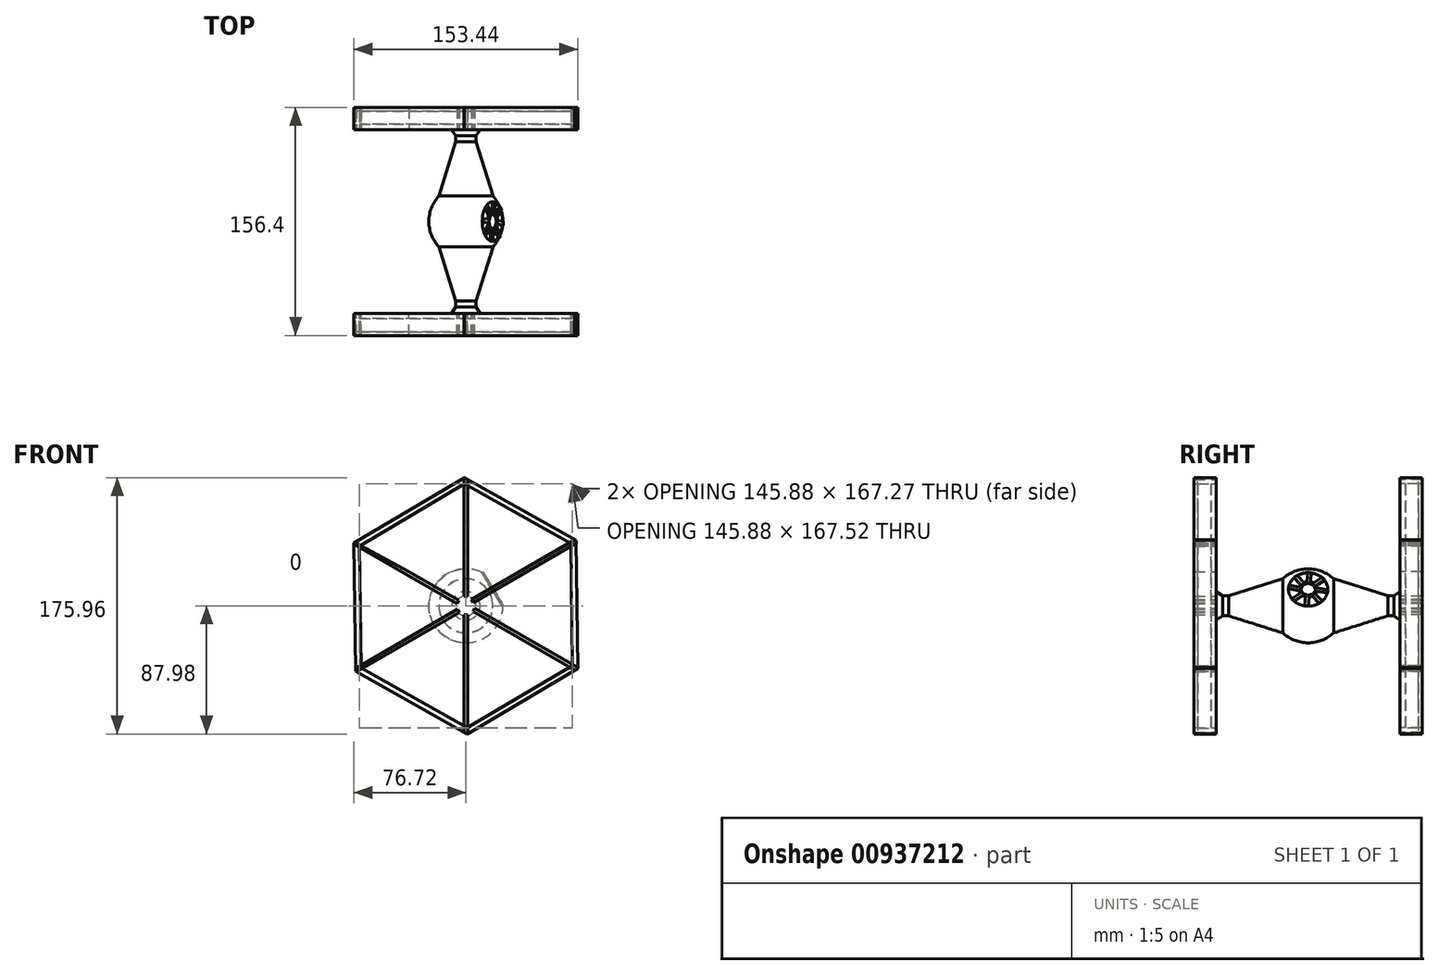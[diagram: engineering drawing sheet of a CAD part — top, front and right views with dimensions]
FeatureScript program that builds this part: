
annotation { "Feature Type Name" : "Feature", "Feature Type Description" : "" }
export const myFeature = defineFeature(function(context is Context, id is Id, definition is map)
    precondition{}
    {
        {
            var Q0;
            Q0=qCreatedBy(makeId("Front.planeOp"),FACE);
            var sketch = newSketch(context, id + "F0", { "sketchPlane" : qUnion([Q0])});
            skArc(sketch, "E0", {"start": v(0, 25.4) * mm, "mid": v(25.4, 0) * mm, "end": v(0, -25.4) * mm});
            skLineSegment(sketch, "E1", {"start": v(0, 25.4) * mm, "end": v(0, -25.4) * mm});
            skSolve(sketch);
        }
        {
            var Q0;
            Q0=qSketchRegion(id+"F0",true);
            var Q1;
            Q1=sQuery(id+"F0.wireOp",EDGE,"E1");
            revolve(context, id + "F1", {"surfaceOperationType" : NewSurfaceOperationType.NEW, "entities" : qUnion([Q0]), "axis" : qUnion([Q1]), "revolveType" : RevolveType.ONE_DIRECTION, "angle" : 180 * degree});
        }
        {
            var Q0;
            Q0=qCreatedBy(makeId("Right.planeOp"),FACE);
            var sketch = newSketch(context, id + "F2", { "sketchPlane" : qUnion([Q0])});
            skLineSegment(sketch, "E2", {"start": v(-62.96, 0) * mm, "end": v(0, 0) * mm});
            skLineSegment(sketch, "E3", {"start": v(-62.96, 0) * mm, "end": v(-62.96, 6.88) * mm});
            skFitSpline(sketch, "E4", {"points": [v(-62.96, 6.88) * mm, v(-54.61, 6.88) * mm, v(-33.5, 12.3) * mm, v(-17.49, 18.56) * mm], "startDerivative": vector(29.42, -2.61) * mm, "endDerivative": vector(41.74, 17.6) * mm});
            skLineSegment(sketch, "E5", {"start": v(-17.49, 18.56) * mm, "end": v(-17.49, 0) * mm});
            skLineSegment(sketch, "E6", {"start": v(-54.61, 6.88) * mm, "end": v(-17.49, 18.56) * mm});
            skLineSegment(sketch, "E7", {"start": v(-54.61, 6.88) * mm, "end": v(-62.96, 6.88) * mm});
            skLineSegment(sketch, "E8", {"start": v(-58.78, 6.88) * mm, "end": v(-62.96, 9.72) * mm});
            skLineSegment(sketch, "E9", {"start": v(-62.96, 6.88) * mm, "end": v(-62.96, 9.72) * mm});
            skSolve(sketch);
        }
        {
            var Q0;
            Q0=qSketchRegion(id+"F2",true);
            var Q1;
            Q1=sQuery(id+"F2.wireOp",EDGE,"E2");
            revolve(context, id + "F3", {"operationType" : NewBodyOperationType.ADD, "surfaceOperationType" : NewSurfaceOperationType.NEW, "entities" : qUnion([Q0]), "axis" : qUnion([Q1]), "revolveType" : RevolveType.FULL});
        }
        {
            var Q0;
            Q0=qCreatedBy(makeId("Front.planeOp"),FACE);
            var sketch = newSketch(context, id + "F4", { "sketchPlane" : qUnion([Q0])});
            skLineSegment(sketch, "E10", {"start": v(18.07, 11.14) * mm, "end": v(0, 0) * mm});
            skSolve(sketch);
        }
        {
            var Q0;
            Q0=makeQuery(id+"F3.opRevolve","SWEPT_FACE",FACE,{"disambiguationData":[OSD([sQuery(id+"F2.wireOp",EDGE,"E3")])]});
            cPlane(context, id + "F5", {"entities" : qUnion([Q0]), "cplaneType" : CPlaneType.OFFSET, "offset" : 0 * mm, "width" : 152.4 * mm, "height" : 152.4 * mm});
        }
        {
            var Q0;
            Q0=qCreatedBy(id+"F5.planeOp",FACE);
            var sketch = newSketch(context, id + "F6", { "sketchPlane" : qUnion([Q0])});
            skCircle(sketch, "E11.cCircle", {"center": v(0, 0) * mm, "radius": 76.2 * mm, "construction": true});
            skLineSegment(sketch, "E11.0", {"start": v(76.62, -43.26) * mm, "end": v(0.84, -87.98) * mm});
            skLineSegment(sketch, "E11.1", {"start": v(0.84, -87.98) * mm, "end": v(-75.78, -44.72) * mm});
            skLineSegment(sketch, "E11.2", {"start": v(-75.78, -44.72) * mm, "end": v(-76.62, 43.26) * mm});
            skLineSegment(sketch, "E11.3", {"start": v(-76.62, 43.26) * mm, "end": v(-0.84, 87.98) * mm});
            skLineSegment(sketch, "E11.4", {"start": v(-0.84, 87.98) * mm, "end": v(75.78, 44.72) * mm});
            skLineSegment(sketch, "E11.5", {"start": v(75.78, 44.72) * mm, "end": v(76.62, -43.26) * mm});
            skPoint(sketch, "E11.0.midPoint", {"position": v(38.73, -65.62) * mm});
            skSolve(sketch);
        }
        {
            var Q0;
            Q0=qSketchRegion(id+"F6",true);
            extrude(context, id + "F7", {"entities" : qUnion([Q0]), "depth" : 12.7 * mm, "offsetDistance" : 25.4 * mm});
        }
        {
            var Q0;
            Q0=makeQuery(id+"F7.opExtrude","CAP_FACE",FACE,{"disambiguationData":[OSD([sQuery(id+"F6.wireOp",EDGE,"E11.0"),sQuery(id+"F6.wireOp",EDGE,"E11.1"),sQuery(id+"F6.wireOp",EDGE,"E11.2"),sQuery(id+"F6.wireOp",EDGE,"E11.3"),sQuery(id+"F6.wireOp",EDGE,"E11.4"),sQuery(id+"F6.wireOp",EDGE,"E11.5")])],"isStart":false});
            shell(context, id + "F8", {"entities" : qUnion([Q0]), "thickness" : 3.66 * mm});
        }
        {
            var Q0;
            Q0=qCreatedBy(id+"F5.planeOp",FACE);
            var sketch = newSketch(context, id + "F9", { "sketchPlane" : qUnion([Q0])});
            skLineSegment(sketch, "E12", {"start": v(0, 92.99) * mm, "end": v(0, 6.47) * mm, "construction": true});
            skLineSegment(sketch, "E13", {"start": v(-80.5, 45.9) * mm, "end": v(-5.53, 2.72) * mm, "construction": true});
            skLineSegment(sketch, "E14", {"start": v(5.53, -2.69) * mm, "end": v(80.5, -45.88) * mm, "construction": true});
            skLineSegment(sketch, "E15", {"start": v(0, -6.03) * mm, "end": v(0, -92.55) * mm});
            skLineSegment(sketch, "E16", {"start": v(-80, -46.75) * mm, "end": v(-5.12, -3.4) * mm, "construction": true});
            skLineSegment(sketch, "E17", {"start": v(4.34, 3.22) * mm, "end": v(79.21, 46.57) * mm, "construction": true});
            skLineSegment(sketch, "E18", {"start": v(-1.27, -6.03) * mm, "end": v(1.27, -6.03) * mm});
            skLineSegment(sketch, "E19", {"start": v(4.9, -3.79) * mm, "end": v(6.17, -1.59) * mm});
            skLineSegment(sketch, "E20", {"start": v(3.7, 4.32) * mm, "end": v(4.97, 2.12) * mm});
            skLineSegment(sketch, "E21", {"start": v(3.7, 4.32) * mm, "end": v(78.58, 47.67) * mm});
            skLineSegment(sketch, "E22", {"start": v(4.97, 2.12) * mm, "end": v(79.85, 45.47) * mm});
            skLineSegment(sketch, "E23", {"start": v(-1.27, 6.47) * mm, "end": v(1.27, 6.47) * mm});
            skLineSegment(sketch, "E24", {"start": v(-6.17, 1.62) * mm, "end": v(-4.9, 3.82) * mm});
            skLineSegment(sketch, "E25", {"start": v(-4.4, -4.44) * mm, "end": v(-5.84, -2.36) * mm});
            skLineSegment(sketch, "E26", {"start": v(-4.9, 3.82) * mm, "end": v(-38.95, 23.43) * mm});
            skLineSegment(sketch, "E27", {"start": v(-6.17, 1.62) * mm, "end": v(-81.14, 44.8) * mm});
            skLineSegment(sketch, "E28", {"start": v(-4.4, -4.44) * mm, "end": v(-79.27, -47.8) * mm});
            skLineSegment(sketch, "E29", {"start": v(-5.84, -2.36) * mm, "end": v(-80, -45.29) * mm});
            skLineSegment(sketch, "E30", {"start": v(4.9, -3.79) * mm, "end": v(79.87, -46.98) * mm});
            skLineSegment(sketch, "E31", {"start": v(6.17, -1.59) * mm, "end": v(81.14, -44.78) * mm});
            skLineSegment(sketch, "E32", {"start": v(-1.27, 6.47) * mm, "end": v(-1.27, 92.99) * mm});
            skLineSegment(sketch, "E33", {"start": v(1.27, 6.47) * mm, "end": v(1.27, 92.99) * mm});
            skLineSegment(sketch, "E34", {"start": v(1.27, -6.03) * mm, "end": v(1.27, -92.55) * mm});
            skLineSegment(sketch, "E35", {"start": v(-1.27, -6.03) * mm, "end": v(-1.27, -92.55) * mm});
            skLineSegment(sketch, "E36", {"start": v(1.27, -92.55) * mm, "end": v(0, -92.55) * mm});
            skLineSegment(sketch, "E37", {"start": v(0, -92.55) * mm, "end": v(-1.27, -92.55) * mm});
            skLineSegment(sketch, "E38", {"start": v(81.14, -44.78) * mm, "end": v(80.5, -45.88) * mm});
            skLineSegment(sketch, "E39", {"start": v(79.87, -46.98) * mm, "end": v(80.5, -45.88) * mm});
            skLineSegment(sketch, "E40", {"start": v(79.21, 46.57) * mm, "end": v(79.85, 45.47) * mm});
            skLineSegment(sketch, "E41", {"start": v(79.21, 46.57) * mm, "end": v(78.58, 47.67) * mm});
            skLineSegment(sketch, "E42", {"start": v(1.27, 92.99) * mm, "end": v(0, 92.99) * mm});
            skLineSegment(sketch, "E43", {"start": v(-1.27, 92.99) * mm, "end": v(0, 92.99) * mm});
            skLineSegment(sketch, "E44", {"start": v(0, 92.99) * mm, "end": v(-1.27, 92.99) * mm});
            skLineSegment(sketch, "E45", {"start": v(-81.14, 44.8) * mm, "end": v(-80.5, 45.9) * mm});
            skLineSegment(sketch, "E46", {"start": v(-38.95, 23.43) * mm, "end": v(-80.5, 45.9) * mm});
            skLineSegment(sketch, "E47", {"start": v(-80, -45.29) * mm, "end": v(-80, -46.75) * mm});
            skLineSegment(sketch, "E48", {"start": v(-79.27, -47.8) * mm, "end": v(-80, -46.75) * mm});
            skSolve(sketch);
        }
        {
            var Q0;
            Q0=qSketchRegion(id+"F9",true);
            extrude(context, id + "F10", {"entities" : qUnion([Q0]), "depth" : 15.24 * mm, "offsetDistance" : 25.4 * mm});
        }
        {
            var Q0;
            Q0=qCreatedBy(id+"F5.planeOp",FACE);
            var sketch = newSketch(context, id + "F11", { "sketchPlane" : qUnion([Q0])});
            skCircle(sketch, "E49.cCircle", {"center": v(0, 0) * mm, "radius": 76.2 * mm, "construction": true});
            skLineSegment(sketch, "E49.0", {"start": v(1.03, -87.98) * mm, "end": v(-75.68, -44.89) * mm});
            skLineSegment(sketch, "E49.1", {"start": v(-75.68, -44.89) * mm, "end": v(-76.71, 43.1) * mm});
            skLineSegment(sketch, "E49.2", {"start": v(-76.71, 43.1) * mm, "end": v(-1.03, 87.98) * mm});
            skLineSegment(sketch, "E49.3", {"start": v(-1.03, 87.98) * mm, "end": v(75.68, 44.89) * mm});
            skLineSegment(sketch, "E49.4", {"start": v(75.68, 44.89) * mm, "end": v(76.71, -43.1) * mm});
            skLineSegment(sketch, "E49.5", {"start": v(76.71, -43.1) * mm, "end": v(1.03, -87.98) * mm});
            skPoint(sketch, "E49.0.midPoint", {"position": v(-37.32, -66.43) * mm});
            skCircle(sketch, "E50.cCircle", {"center": v(0, 0) * mm, "radius": 72.43 * mm, "construction": true});
            skLineSegment(sketch, "E50.0", {"start": v(72.94, -40.93) * mm, "end": v(1.03, -83.63) * mm});
            skLineSegment(sketch, "E50.1", {"start": v(1.03, -83.63) * mm, "end": v(-71.92, -42.7) * mm});
            skLineSegment(sketch, "E50.2", {"start": v(-71.92, -42.7) * mm, "end": v(-72.94, 40.93) * mm});
            skLineSegment(sketch, "E50.3", {"start": v(-72.94, 40.93) * mm, "end": v(-1.03, 83.63) * mm});
            skLineSegment(sketch, "E50.4", {"start": v(-1.03, 83.63) * mm, "end": v(71.92, 42.7) * mm});
            skLineSegment(sketch, "E50.5", {"start": v(71.92, 42.7) * mm, "end": v(72.94, -40.93) * mm});
            skPoint(sketch, "E50.0.midPoint", {"position": v(36.98, -62.28) * mm});
            skLineSegment(sketch, "E51", {"start": v(0, 0) * mm, "end": v(-1.03, 83.63) * mm, "construction": true});
            skSolve(sketch);
        }
        {
            var Q0;
            Q0=qSketchRegion(id+"F11",true);
            extrude(context, id + "F12", {"entities" : qUnion([Q0]), "depth" : 15.24 * mm, "offsetDistance" : 25.4 * mm});
        }
        {
            var Q0;
            Q0=qCreatedBy(id+"F5.planeOp",FACE);
            var sketch = newSketch(context, id + "F13", { "sketchPlane" : qUnion([Q0])});
            skCircle(sketch, "E52.cCircle", {"center": v(0, 0) * mm, "radius": 76.2 * mm, "construction": true});
            skLineSegment(sketch, "E52.0", {"start": v(1.05, -87.98) * mm, "end": v(-75.67, -44.9) * mm});
            skLineSegment(sketch, "E52.1", {"start": v(-75.67, -44.9) * mm, "end": v(-76.72, 43.08) * mm});
            skLineSegment(sketch, "E52.2", {"start": v(-76.72, 43.08) * mm, "end": v(-1.05, 87.98) * mm});
            skLineSegment(sketch, "E52.3", {"start": v(-1.05, 87.98) * mm, "end": v(75.67, 44.9) * mm});
            skLineSegment(sketch, "E52.4", {"start": v(75.67, 44.9) * mm, "end": v(76.72, -43.08) * mm});
            skLineSegment(sketch, "E52.5", {"start": v(76.72, -43.08) * mm, "end": v(1.05, -87.98) * mm});
            skPoint(sketch, "E52.0.midPoint", {"position": v(-37.31, -66.44) * mm});
            skCircle(sketch, "E53.cCircle", {"center": v(0, 0) * mm, "radius": 151.68 * mm, "construction": true});
            skLineSegment(sketch, "E53.0", {"start": v(-149.87, -90.64) * mm, "end": v(-153.43, 84.47) * mm});
            skLineSegment(sketch, "E53.1", {"start": v(-153.43, 84.47) * mm, "end": v(-3.56, 175.11) * mm});
            skLineSegment(sketch, "E53.2", {"start": v(-3.56, 175.11) * mm, "end": v(149.87, 90.64) * mm});
            skLineSegment(sketch, "E53.3", {"start": v(149.87, 90.64) * mm, "end": v(153.43, -84.47) * mm});
            skLineSegment(sketch, "E53.4", {"start": v(153.43, -84.47) * mm, "end": v(3.56, -175.11) * mm});
            skLineSegment(sketch, "E53.5", {"start": v(3.56, -175.11) * mm, "end": v(-149.87, -90.64) * mm});
            skPoint(sketch, "E53.0.midPoint", {"position": v(-151.65, -3.09) * mm});
            skSolve(sketch);
        }
        {
            var Q0;
            Q0=qSketchRegion(id+"F13",true);
            extrude(context, id + "F14", {"entities" : qUnion([Q0]), "operationType" : NewBodyOperationType.REMOVE, "depth" : 101.6 * mm, "offsetDistance" : 25.4 * mm});
        }
        {
            var Q0;
            Q0=makeQuery(id+"F1.opRevolve","SWEPT_BODY",BODY,{"disambiguationData":[OSD([sQuery(id+"F0.wireOp",EDGE,"E0"),sQuery(id+"F0.wireOp",EDGE,"E1")])]});
            var Q1;
            Q1=makeQuery(id+"F12.opExtrude","SWEPT_BODY",BODY,{"disambiguationData":[OSD([sQuery(id+"F11.wireOp",EDGE,"E49.0"),sQuery(id+"F11.wireOp",EDGE,"E49.1"),sQuery(id+"F11.wireOp",EDGE,"E49.2"),sQuery(id+"F11.wireOp",EDGE,"E49.3"),sQuery(id+"F11.wireOp",EDGE,"E49.4"),sQuery(id+"F11.wireOp",EDGE,"E49.5"),sQuery(id+"F11.wireOp",EDGE,"E50.0"),sQuery(id+"F11.wireOp",EDGE,"E50.1"),sQuery(id+"F11.wireOp",EDGE,"E50.2"),sQuery(id+"F11.wireOp",EDGE,"E50.3"),sQuery(id+"F11.wireOp",EDGE,"E50.4"),sQuery(id+"F11.wireOp",EDGE,"E50.5")])]});
            var Q2;
            Q2=makeQuery(id+"F10.opExtrude","SWEPT_BODY",BODY,{"disambiguationData":[OSD([sQuery(id+"F9.wireOp",EDGE,"E20"),sQuery(id+"F9.wireOp",EDGE,"E21"),sQuery(id+"F9.wireOp",EDGE,"E22"),sQuery(id+"F9.wireOp",EDGE,"E40"),sQuery(id+"F9.wireOp",EDGE,"E41")])]});
            var Q3;
            Q3=makeQuery(id+"F7.opExtrude","SWEPT_BODY",BODY,{"disambiguationData":[OSD([sQuery(id+"F6.wireOp",EDGE,"E11.0"),sQuery(id+"F6.wireOp",EDGE,"E11.1"),sQuery(id+"F6.wireOp",EDGE,"E11.2"),sQuery(id+"F6.wireOp",EDGE,"E11.3"),sQuery(id+"F6.wireOp",EDGE,"E11.4"),sQuery(id+"F6.wireOp",EDGE,"E11.5")])]});
            var Q4;
            Q4=makeQuery(id+"F10.opExtrude","SWEPT_BODY",BODY,{"disambiguationData":[OSD([sQuery(id+"F9.wireOp",EDGE,"E19"),sQuery(id+"F9.wireOp",EDGE,"E30"),sQuery(id+"F9.wireOp",EDGE,"E31"),sQuery(id+"F9.wireOp",EDGE,"E38"),sQuery(id+"F9.wireOp",EDGE,"E39")])]});
            var Q5;
            Q5=makeQuery(id+"F10.opExtrude","SWEPT_BODY",BODY,{"disambiguationData":[OSD([sQuery(id+"F9.wireOp",EDGE,"E18"),sQuery(id+"F9.wireOp",EDGE,"E34"),sQuery(id+"F9.wireOp",EDGE,"E35"),sQuery(id+"F9.wireOp",EDGE,"E36"),sQuery(id+"F9.wireOp",EDGE,"E37")])]});
            var Q6;
            Q6=makeQuery(id+"F10.opExtrude","SWEPT_BODY",BODY,{"disambiguationData":[OSD([sQuery(id+"F9.wireOp",EDGE,"E24"),sQuery(id+"F9.wireOp",EDGE,"E26"),sQuery(id+"F9.wireOp",EDGE,"E27"),sQuery(id+"F9.wireOp",EDGE,"E45"),sQuery(id+"F9.wireOp",EDGE,"E46")])]});
            var Q7;
            Q7=makeQuery(id+"F10.opExtrude","SWEPT_BODY",BODY,{"disambiguationData":[OSD([sQuery(id+"F9.wireOp",EDGE,"E23"),sQuery(id+"F9.wireOp",EDGE,"E32"),sQuery(id+"F9.wireOp",EDGE,"E33"),sQuery(id+"F9.wireOp",EDGE,"E42"),sQuery(id+"F9.wireOp",EDGE,"E44")])]});
            var Q8;
            Q8=makeQuery(id+"F10.opExtrude","SWEPT_BODY",BODY,{"disambiguationData":[OSD([sQuery(id+"F9.wireOp",EDGE,"E25"),sQuery(id+"F9.wireOp",EDGE,"E28"),sQuery(id+"F9.wireOp",EDGE,"E29"),sQuery(id+"F9.wireOp",EDGE,"E47"),sQuery(id+"F9.wireOp",EDGE,"E48")])]});
            var Q9;
            Q9=qCreatedBy(makeId("Front.planeOp"),FACE);
            mirror(context, id + "F15", {"entities" : qUnion([Q0, Q1, Q2, Q3, Q4, Q5, Q6, Q7, Q8]), "mirrorPlane" : qUnion([Q9])});
        }
        {
            var Q0;
            Q0=sQuery(id+"F4.wireOp",VERTEX,"E10.start");
            var Q1;
            Q1=sQuery(id+"F4.wireOp",EDGE,"E10");
            cPlane(context, id + "F16", {"entities" : qUnion([Q0, Q1]), "cplaneType" : CPlaneType.CURVE_POINT, "offset" : 25.4 * mm, "width" : 152.4 * mm, "height" : 152.4 * mm});
        }
        {
            var Q0;
            Q0=qCreatedBy(id+"F16.planeOp",FACE);
            var sketch = newSketch(context, id + "F17", { "sketchPlane" : qUnion([Q0])});
            skCircle(sketch, "E54", {"center": v(0, 0) * mm, "radius": 13.5 * mm});
            skSolve(sketch);
        }
        {
            var Q0;
            Q0=qSketchRegion(id+"F17",true);
            extrude(context, id + "F18", {"entities" : qUnion([Q0]), "operationType" : NewBodyOperationType.REMOVE, "oppositeDirection" : true, "depth" : 25.4 * mm, "offsetDistance" : 25.4 * mm});
        }
        {
            var Q0;
            Q0=qCreatedBy(id+"F16.planeOp",FACE);
            var sketch = newSketch(context, id + "F19", { "sketchPlane" : qUnion([Q0])});
            skCircle(sketch, "E55.cCircle", {"center": v(0, 0) * mm, "radius": 6.1 * mm, "construction": true});
            skLineSegment(sketch, "E55.0", {"start": v(0.45, -6.6) * mm, "end": v(-4.34, -4.98) * mm});
            skLineSegment(sketch, "E55.1", {"start": v(-4.34, -4.98) * mm, "end": v(-6.6, -0.45) * mm});
            skLineSegment(sketch, "E55.2", {"start": v(-6.6, -0.45) * mm, "end": v(-4.98, 4.34) * mm});
            skLineSegment(sketch, "E55.3", {"start": v(-4.98, 4.34) * mm, "end": v(-0.45, 6.6) * mm});
            skLineSegment(sketch, "E55.4", {"start": v(-0.45, 6.6) * mm, "end": v(4.34, 4.98) * mm});
            skLineSegment(sketch, "E55.5", {"start": v(4.34, 4.98) * mm, "end": v(6.6, 0.45) * mm});
            skLineSegment(sketch, "E55.6", {"start": v(6.6, 0.45) * mm, "end": v(4.98, -4.34) * mm});
            skLineSegment(sketch, "E55.7", {"start": v(4.98, -4.34) * mm, "end": v(0.45, -6.6) * mm});
            skPoint(sketch, "E55.0.midPoint", {"position": v(-1.95, -5.78) * mm});
            skLineSegment(sketch, "E56", {"start": v(-0.45, 6.6) * mm, "end": v(-0.87, 13.38) * mm, "construction": true});
            skLineSegment(sketch, "E57", {"start": v(4.34, 4.98) * mm, "end": v(8.62, 10.27) * mm, "construction": true});
            skLineSegment(sketch, "E58", {"start": v(-4.98, 4.34) * mm, "end": v(-10.46, 8.47) * mm, "construction": true});
            skLineSegment(sketch, "E59", {"start": v(-6.6, -0.45) * mm, "end": v(-13.35, -1.73) * mm, "construction": true});
            skLineSegment(sketch, "E60", {"start": v(-4.34, -4.98) * mm, "end": v(-8.67, -10.4) * mm, "construction": true});
            skLineSegment(sketch, "E61", {"start": v(0.45, -6.6) * mm, "end": v(1.08, -13.42) * mm, "construction": true});
            skLineSegment(sketch, "E62", {"start": v(4.98, -4.34) * mm, "end": v(10.28, -8.68) * mm, "construction": true});
            skLineSegment(sketch, "E63", {"start": v(6.6, 0.45) * mm, "end": v(13.35, 1.77) * mm, "construction": true});
            skLineSegment(sketch, "E64", {"start": v(7.59, 11.13) * mm, "end": v(9.66, 9.42) * mm});
            skLineSegment(sketch, "E65", {"start": v(7.59, 11.13) * mm, "end": v(2.92, 5.46) * mm});
            skLineSegment(sketch, "E66", {"start": v(9.66, 9.42) * mm, "end": v(5, 3.66) * mm});
            skLineSegment(sketch, "E67", {"start": v(-2.1, 13.3) * mm, "end": v(0.37, 13.45) * mm});
            skLineSegment(sketch, "E68", {"start": v(-2.1, 13.3) * mm, "end": v(-1.65, 6) * mm});
            skLineSegment(sketch, "E69", {"start": v(0.37, 13.45) * mm, "end": v(0.8, 6.17) * mm});
            skCircle(sketch, "E70.cCircle", {"center": v(0, 0) * mm, "radius": 4.83 * mm, "construction": true});
            skLineSegment(sketch, "E70.0", {"start": v(4, -3.37) * mm, "end": v(0.45, -5.21) * mm});
            skLineSegment(sketch, "E70.1", {"start": v(0.45, -5.21) * mm, "end": v(-3.37, -4) * mm});
            skLineSegment(sketch, "E70.2", {"start": v(-3.37, -4) * mm, "end": v(-5.21, -0.45) * mm});
            skLineSegment(sketch, "E70.3", {"start": v(-5.21, -0.45) * mm, "end": v(-4, 3.37) * mm});
            skLineSegment(sketch, "E70.4", {"start": v(-4, 3.37) * mm, "end": v(-0.45, 5.21) * mm});
            skLineSegment(sketch, "E70.5", {"start": v(-0.45, 5.21) * mm, "end": v(3.37, 4) * mm});
            skLineSegment(sketch, "E70.6", {"start": v(3.37, 4) * mm, "end": v(5.21, 0.45) * mm});
            skLineSegment(sketch, "E70.7", {"start": v(5.21, 0.45) * mm, "end": v(4, -3.37) * mm});
            skPoint(sketch, "E70.0.midPoint", {"position": v(2.23, -4.3) * mm});
            skLineSegment(sketch, "E71", {"start": v(-11.23, 7.47) * mm, "end": v(-9.7, 9.47) * mm});
            skLineSegment(sketch, "E72", {"start": v(-9.7, 9.47) * mm, "end": v(-3.79, 4.93) * mm});
            skLineSegment(sketch, "E73", {"start": v(-11.23, 7.47) * mm, "end": v(-5.43, 3) * mm});
            skLineSegment(sketch, "E74", {"start": v(-13.57, -0.58) * mm, "end": v(-13.13, -2.87) * mm});
            skLineSegment(sketch, "E75", {"start": v(-13.13, -2.87) * mm, "end": v(-6.05, -1.53) * mm});
            skLineSegment(sketch, "E76", {"start": v(-13.57, -0.58) * mm, "end": v(-6.16, 0.82) * mm});
            skLineSegment(sketch, "E77", {"start": v(-9.64, -9.57) * mm, "end": v(-7.71, -11.23) * mm});
            skLineSegment(sketch, "E78", {"start": v(-9.64, -9.57) * mm, "end": v(-4.83, -4) * mm});
            skLineSegment(sketch, "E79", {"start": v(-7.71, -11.23) * mm, "end": v(-3.06, -5.4) * mm});
            skLineSegment(sketch, "E80", {"start": v(2.34, -13.3) * mm, "end": v(-0.19, -13.53) * mm});
            skLineSegment(sketch, "E81", {"start": v(-0.19, -13.53) * mm, "end": v(-0.87, -6.15) * mm});
            skLineSegment(sketch, "E82", {"start": v(2.34, -13.3) * mm, "end": v(1.67, -5.99) * mm});
            skLineSegment(sketch, "E83", {"start": v(9.46, -9.68) * mm, "end": v(11.1, -7.67) * mm});
            skLineSegment(sketch, "E84", {"start": v(9.46, -9.68) * mm, "end": v(3.7, -4.98) * mm});
            skLineSegment(sketch, "E85", {"start": v(11.1, -7.67) * mm, "end": v(5.42, -3.03) * mm});
            skLineSegment(sketch, "E86", {"start": v(13.1, 3.01) * mm, "end": v(13.6, 0.52) * mm});
            skLineSegment(sketch, "E87", {"start": v(13.1, 3.01) * mm, "end": v(6, 1.63) * mm});
            skLineSegment(sketch, "E88", {"start": v(13.6, 0.52) * mm, "end": v(6.13, -0.93) * mm});
            skSolve(sketch);
        }
        {
            var Q0;
            Q0=qSketchRegion(id+"F19",true);
            extrude(context, id + "F20", {"entities" : qUnion([Q0]), "operationType" : NewBodyOperationType.ADD, "oppositeDirection" : true, "depth" : 0.76 * mm, "offsetDistance" : 25.4 * mm});
        }
    });
